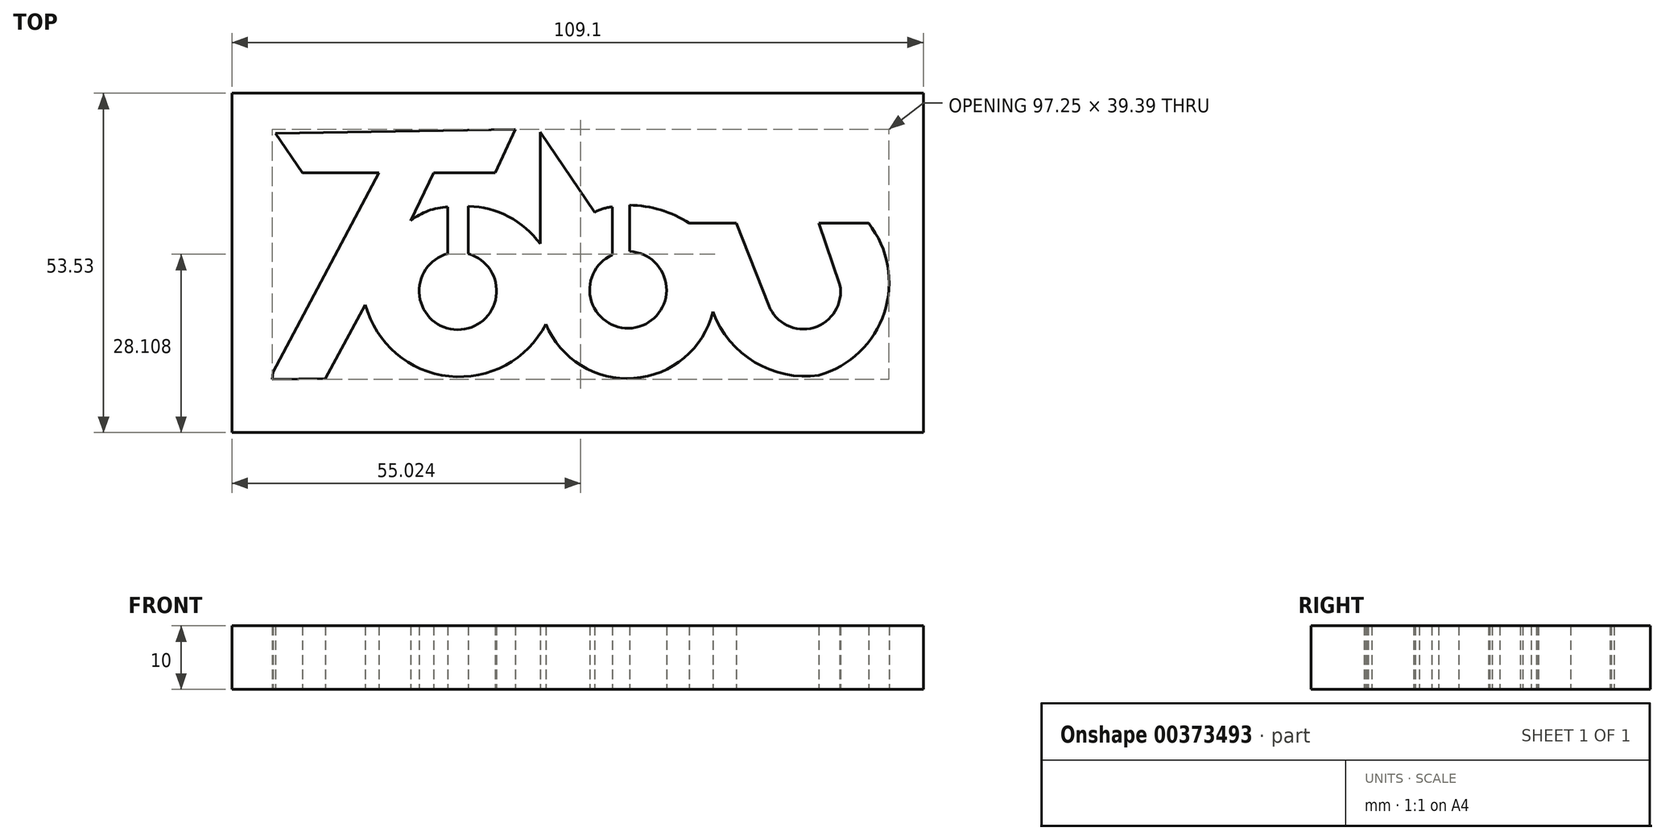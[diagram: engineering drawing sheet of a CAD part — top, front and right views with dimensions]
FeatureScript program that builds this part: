
annotation { "Feature Type Name" : "Feature", "Feature Type Description" : "" }
export const myFeature = defineFeature(function(context is Context, id is Id, definition is map)
    precondition{}
    {
        {
            var Q0;
            Q0=qCreatedBy(makeId("Top.planeOp"),FACE);
            var sketch = newSketch(context, id + "F0", { "sketchPlane" : qUnion([Q0])});
            skLineSegment(sketch, "E0", {"start": v(-43.05, -21.56) * mm, "end": v(-26.36, 9.85) * mm});
            skLineSegment(sketch, "E1", {"start": v(-26.36, 9.85) * mm, "end": v(-38.39, 9.85) * mm});
            skLineSegment(sketch, "E2", {"start": v(-38.39, 9.85) * mm, "end": v(-42.7, 16.04) * mm});
            skLineSegment(sketch, "E3", {"start": v(-42.7, 16.04) * mm, "end": v(-4.8, 16.69) * mm});
            skLineSegment(sketch, "E4", {"start": v(-4.8, 16.69) * mm, "end": v(-8, 9.85) * mm});
            skLineSegment(sketch, "E5", {"start": v(-8, 9.85) * mm, "end": v(-17.7, 9.85) * mm});
            skLineSegment(sketch, "E6", {"start": v(-17.7, 9.85) * mm, "end": v(-21.31, 2.31) * mm});
            skPoint(sketch, "E7.second.point", {"position": v(-0.9, -1.34) * mm});
            skPoint(sketch, "E7.third.point", {"position": v(-19.7, -20.93) * mm});
            skLineSegment(sketch, "E8", {"start": v(-0.9, -1.34) * mm, "end": v(-0.9, 16.27) * mm});
            skLineSegment(sketch, "E9", {"start": v(-0.9, 16.27) * mm, "end": v(7.68, 3.63) * mm});
            skLineSegment(sketch, "E10", {"start": v(22.63, 1.9) * mm, "end": v(30.03, 1.9) * mm});
            skLineSegment(sketch, "E11", {"start": v(30.03, 1.9) * mm, "end": v(35.16, -11.1) * mm});
            skArc(sketch, "E12", {"start": v(35.16, -11.1) * mm, "mid": v(42.26, -14.58) * mm, "end": v(46.39, -7.83) * mm});
            skLineSegment(sketch, "E13", {"start": v(46.39, -7.83) * mm, "end": v(43.08, 1.9) * mm});
            skLineSegment(sketch, "E14", {"start": v(43.08, 1.9) * mm, "end": v(50.91, 1.9) * mm});
            skArc(sketch, "E15", {"start": v(43.08, -22.09) * mm, "mid": v(53.4, -12.18) * mm, "end": v(50.91, 1.9) * mm});
            skArc(sketch, "E16", {"start": v(26.36, -12.07) * mm, "mid": v(32.95, -20.03) * mm, "end": v(43.08, -22.09) * mm});
            skArc(sketch, "E17", {"start": v(0, -14.01) * mm, "mid": v(13.88, -22.57) * mm, "end": v(26.36, -12.07) * mm});
            skArc(sketch, "E18", {"start": v(-28.48, -10.96) * mm, "mid": v(-15.28, -22.25) * mm, "end": v(0, -14.01) * mm});
            skLineSegment(sketch, "E19", {"start": v(-28.48, -10.96) * mm, "end": v(-34.82, -22.6) * mm});
            skLineSegment(sketch, "E20", {"start": v(-34.82, -22.6) * mm, "end": v(-43.14, -22.7) * mm});
            skLineSegment(sketch, "E21", {"start": v(-43.14, -22.7) * mm, "end": v(-43.05, -21.56) * mm});
            skPoint(sketch, "E22.first.point", {"position": v(-19.49, -7.43) * mm});
            skPoint(sketch, "E22.second.point", {"position": v(-7.8, -9.64) * mm});
            skPoint(sketch, "E22.third.point", {"position": v(-13.4, -2.9) * mm});
            skPoint(sketch, "E23.first.point", {"position": v(6.73, -8.07) * mm});
            skPoint(sketch, "E23.second.point", {"position": v(18.68, -9.04) * mm});
            skPoint(sketch, "E23.third.point", {"position": v(12.7, -2.64) * mm});
            skLineSegment(sketch, "E24", {"start": v(-15.46, 4.44) * mm, "end": v(-15.46, -2.9) * mm});
            skLineSegment(sketch, "E25", {"start": v(-12.22, 4.59) * mm, "end": v(-12.22, -2.93) * mm});
            skArc(sketch, "E26", {"start": v(-15.46, -2.9) * mm, "mid": v(-13.94, -14.91) * mm, "end": v(-12.22, -2.93) * mm});
            skArc(sketch, "E27", {"start": v(-15.46, 4.44) * mm, "mid": v(-18.56, 3.85) * mm, "end": v(-21.31, 2.31) * mm});
            skArc(sketch, "E28", {"start": v(-0.9, -1.34) * mm, "mid": v(-5.88, 2.93) * mm, "end": v(-12.22, 4.59) * mm});
            skLineSegment(sketch, "E29", {"start": v(10.46, 4.45) * mm, "end": v(10.46, -3.1) * mm});
            skLineSegment(sketch, "E30", {"start": v(13.19, 4.75) * mm, "end": v(13.19, -2.56) * mm});
            skArc(sketch, "E31", {"start": v(10.46, -3.1) * mm, "mid": v(14.14, -14.56) * mm, "end": v(13.19, -2.56) * mm});
            skArc(sketch, "E32", {"start": v(10.46, 4.45) * mm, "mid": v(9.03, 4.2) * mm, "end": v(7.68, 3.63) * mm});
            skArc(sketch, "E33", {"start": v(22.63, 1.9) * mm, "mid": v(18.11, 3.98) * mm, "end": v(13.19, 4.75) * mm});
            skSolve(sketch);
        }
        {
            var Q0;
            Q0=qCreatedBy(makeId("Top.planeOp"),FACE);
            var sketch = newSketch(context, id + "F1", { "sketchPlane" : qUnion([Q0])});
            skLineSegment(sketch, "E34.bottom", {"start": v(-49.54, 22.4) * mm, "end": v(59.56, 22.4) * mm});
            skLineSegment(sketch, "E34.top", {"start": v(-49.54, -31.12) * mm, "end": v(59.56, -31.12) * mm});
            skLineSegment(sketch, "E34.left", {"start": v(-49.54, 22.4) * mm, "end": v(-49.54, -31.12) * mm});
            skLineSegment(sketch, "E34.right", {"start": v(59.56, 22.4) * mm, "end": v(59.56, -31.12) * mm});
            skSolve(sketch);
        }
        {
            var Q0;
            Q0 = qSketchRegion(id + "F1", true);
            extrude(context, id + "F2", {"entities" : qUnion([Q0]), "depth" : 10 * mm});
        }
        {
            var Q0;
            Q0 = qSketchRegion(id + "F0", true);
            extrude(context, id + "F3", {"entities" : qUnion([Q0]), "operationType" : NewBodyOperationType.REMOVE, "depth" : 20 * mm});
        }
    });
